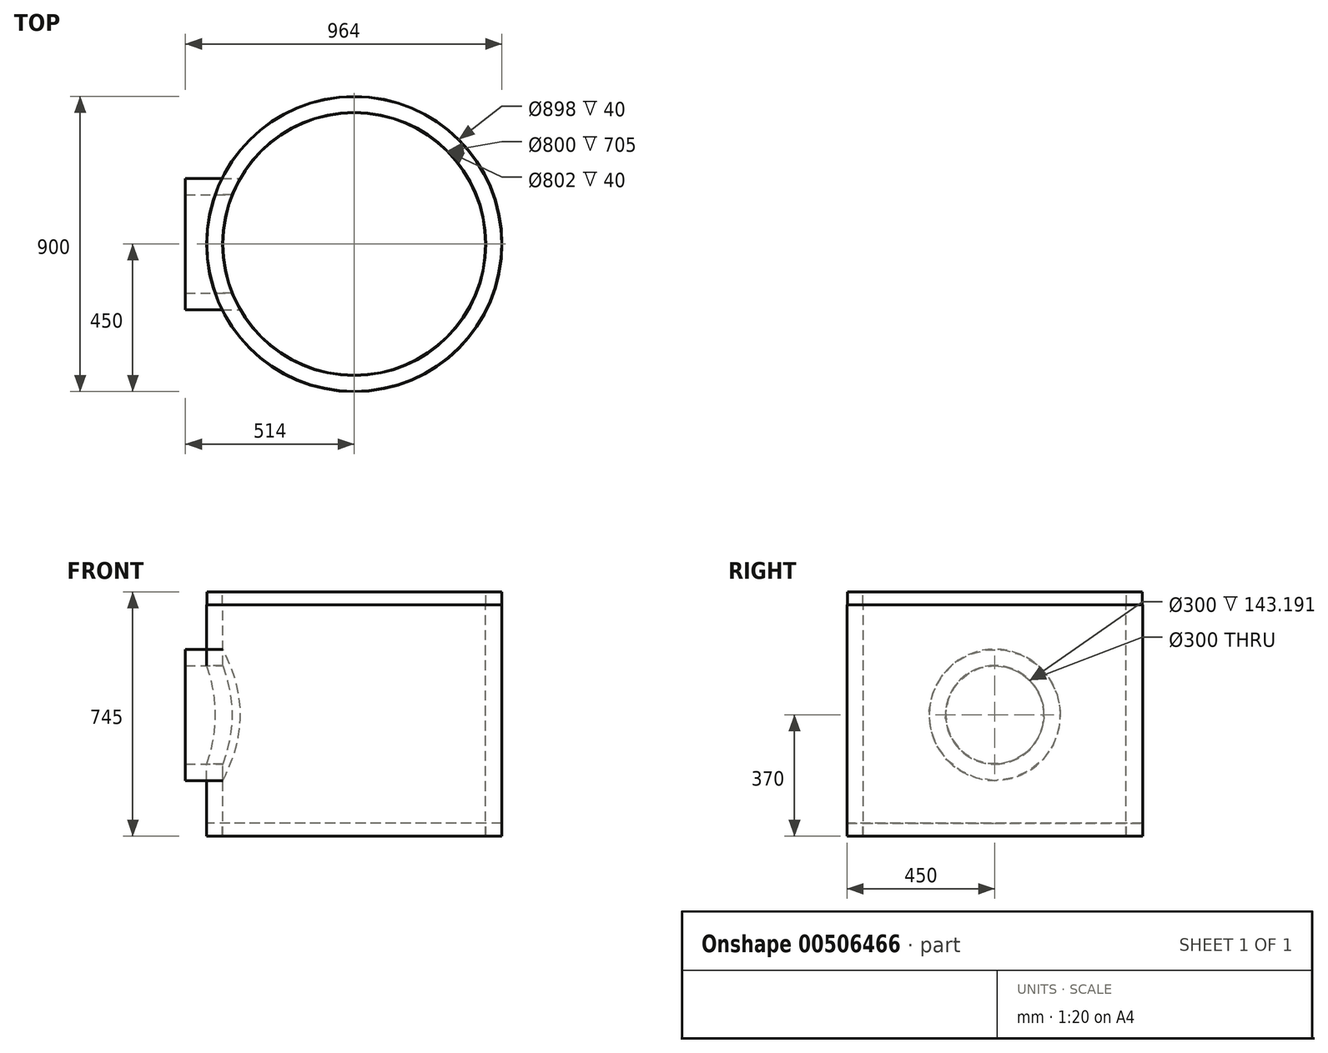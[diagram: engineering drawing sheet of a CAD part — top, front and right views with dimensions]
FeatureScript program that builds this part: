
annotation { "Feature Type Name" : "Feature", "Feature Type Description" : "" }
export const myFeature = defineFeature(function(context is Context, id is Id, definition is map)
    precondition{}
    {
        {
            var Q0;
            Q0=qCreatedBy(makeId("Front.planeOp"),FACE);
            var sketch = newSketch(context, id + "F0", { "sketchPlane" : qUnion([Q0])});
            skLineSegment(sketch, "E0", {"start": v(0, 722.18) * mm, "end": v(0, -793.11) * mm, "construction": true});
            skLineSegment(sketch, "E1", {"start": v(-400, -370) * mm, "end": v(-400, 335) * mm});
            skLineSegment(sketch, "E2", {"start": v(-400, 335) * mm, "end": v(-401, 335) * mm});
            skLineSegment(sketch, "E3", {"start": v(-401, 335) * mm, "end": v(-401, 375) * mm});
            skLineSegment(sketch, "E4", {"start": v(-401, 375) * mm, "end": v(-449, 375) * mm});
            skLineSegment(sketch, "E5", {"start": v(-449, 375) * mm, "end": v(-449, 335) * mm});
            skLineSegment(sketch, "E6", {"start": v(-449, 335) * mm, "end": v(-450, 335) * mm});
            skLineSegment(sketch, "E7", {"start": v(-450, 335) * mm, "end": v(-450, -370) * mm});
            skLineSegment(sketch, "E8", {"start": v(-450, -370) * mm, "end": v(-449, -370) * mm});
            skLineSegment(sketch, "E9", {"start": v(-449, -370) * mm, "end": v(-449, -330) * mm});
            skLineSegment(sketch, "E10", {"start": v(-449, -330) * mm, "end": v(-401, -330) * mm});
            skLineSegment(sketch, "E11", {"start": v(-401, -330) * mm, "end": v(-401, -370) * mm});
            skLineSegment(sketch, "E12", {"start": v(-401, -370) * mm, "end": v(-400, -370) * mm});
            skLineSegment(sketch, "E13", {"start": v(0, 0) * mm, "end": v(-928, 0) * mm, "construction": true});
            skLineSegment(sketch, "E14", {"start": v(0, -150) * mm, "end": v(-514, -150) * mm});
            skLineSegment(sketch, "E15", {"start": v(-514, -150) * mm, "end": v(-514, -200) * mm});
            skLineSegment(sketch, "E16", {"start": v(-514, -200) * mm, "end": v(0, -200) * mm});
            skLineSegment(sketch, "E17", {"start": v(0, -200) * mm, "end": v(0, -150) * mm});
            skLineSegment(sketch, "E18", {"start": v(-514, -150) * mm, "end": v(-514, 0) * mm});
            skLineSegment(sketch, "E19", {"start": v(-514, 0) * mm, "end": v(-464, 0) * mm});
            skLineSegment(sketch, "E20", {"start": v(-464, 0) * mm, "end": v(-464, -150) * mm});
            skSolve(sketch);
        }
        {
            var Q0;
            {var subQ0=sQuery(id+"F0.wireOp",EDGE,"E2");Q0=makeQuery(id+"F0.imprint","IMPRINT",FACE,{"disambiguationData":[TD([[makeQuery(id+"F0.imprint","IMPRINT",EDGE,{"derivedFrom":subQ0}),1.0]])]});}
            var Q1;
            {var subQ0=sQuery(id+"F0.wireOp",EDGE,"E16");var subQ1=sQuery(id+"F0.wireOp",EDGE,"E1");var subQ2=makeQuery(id+"F0.imprint","INTERSECT",VERTEX,{"derivedFrom":[subQ1,subQ0]});Q1=makeQuery(id+"F0.imprint","IMPRINT",FACE,{"disambiguationData":[TD([[makeQuery(id+"F0.imprint","IMPRINT",EDGE,{"disambiguationData":[TD([[subQ2,-1.0]])],"derivedFrom":subQ1}),1.0]])]});}
            var Q2;
            {var subQ0=sQuery(id+"F0.wireOp",EDGE,"E8");Q2=makeQuery(id+"F0.imprint","IMPRINT",FACE,{"disambiguationData":[TD([[makeQuery(id+"F0.imprint","IMPRINT",EDGE,{"derivedFrom":subQ0}),1.0]])]});}
            var Q3;
            Q3=sQuery(id+"F0.wireOp",EDGE,"E0");
            revolve(context, id + "F1", {"entities" : qUnion([Q0, Q1, Q2]), "axis" : qUnion([Q3]), "revolveType" : RevolveType.FULL});
        }
        {
            var Q0;
            {var subQ0=sQuery(id+"F0.wireOp",EDGE,"E18");Q0=makeQuery(id+"F0.imprint","IMPRINT",FACE,{"disambiguationData":[TD([[makeQuery(id+"F0.imprint","IMPRINT",EDGE,{"derivedFrom":subQ0}),-1.0]])]});}
            var Q1;
            {var subQ0=sQuery(id+"F0.wireOp",EDGE,"E15");Q1=makeQuery(id+"F0.imprint","IMPRINT",FACE,{"disambiguationData":[TD([[makeQuery(id+"F0.imprint","IMPRINT",EDGE,{"derivedFrom":subQ0}),1.0]])]});}
            var Q2;
            {var subQ0=sQuery(id+"F0.wireOp",EDGE,"E16");var subQ1=sQuery(id+"F0.wireOp",EDGE,"E1");var subQ2=makeQuery(id+"F0.imprint","INTERSECT",VERTEX,{"derivedFrom":[subQ1,subQ0]});Q2=makeQuery(id+"F0.imprint","IMPRINT",FACE,{"disambiguationData":[TD([[makeQuery(id+"F0.imprint","IMPRINT",EDGE,{"disambiguationData":[TD([[subQ2,-1.0]])],"derivedFrom":subQ1}),1.0]])]});}
            var Q3;
            {var subQ5=sQuery(id+"F0.wireOp",EDGE,"E17");Q3=makeQuery(id+"F0.imprint","IMPRINT",FACE,{"disambiguationData":[TD([[makeQuery(id+"F0.imprint","IMPRINT",EDGE,{"derivedFrom":subQ5}),1.0]])]});}
            var Q4;
            Q4=sQuery(id+"F0.wireOp",EDGE,"E13");
            revolve(context, id + "F2", {"entities" : qUnion([Q0, Q1, Q2, Q3]), "axis" : qUnion([Q4]), "revolveType" : RevolveType.FULL});
        }
        {
            var Q0;
            Q0=makeQuery(id+"F2.opRevolve","SWEPT_FACE",FACE,{"disambiguationData":[OSD([sQuery(id+"F0.wireOp",EDGE,"E15"),sQuery(id+"F0.wireOp",EDGE,"E18")])]});
            var sketch = newSketch(context, id + "F3", { "sketchPlane" : qUnion([Q0])});
            skCircle(sketch, "E21", {"center": v(0, 0) * mm, "radius": 150 * mm});
            skSolve(sketch);
        }
        {
            var Q0;
            Q0=qSketchRegion(id+"F3",true);
            extrude(context, id + "F4", {"entities" : qUnion([Q0]), "operationType" : NewBodyOperationType.REMOVE, "oppositeDirection" : true, "depth" : 600 * mm});
        }
        {
            var Q0;
            Q0=makeQuery(id+"F1.opRevolve","SWEPT_FACE",FACE,{"disambiguationData":[OSD([sQuery(id+"F0.wireOp",EDGE,"E4")])]});
            var sketch = newSketch(context, id + "F5", { "sketchPlane" : qUnion([Q0])});
            skCircle(sketch, "E22", {"center": v(0, 0) * mm, "radius": 400 * mm});
            skSolve(sketch);
        }
        {
            var Q0;
            Q0=qSketchRegion(id+"F5",true);
            extrude(context, id + "F6", {"entities" : qUnion([Q0]), "operationType" : NewBodyOperationType.REMOVE, "oppositeDirection" : true, "depth" : 1200 * mm});
        }
    });
